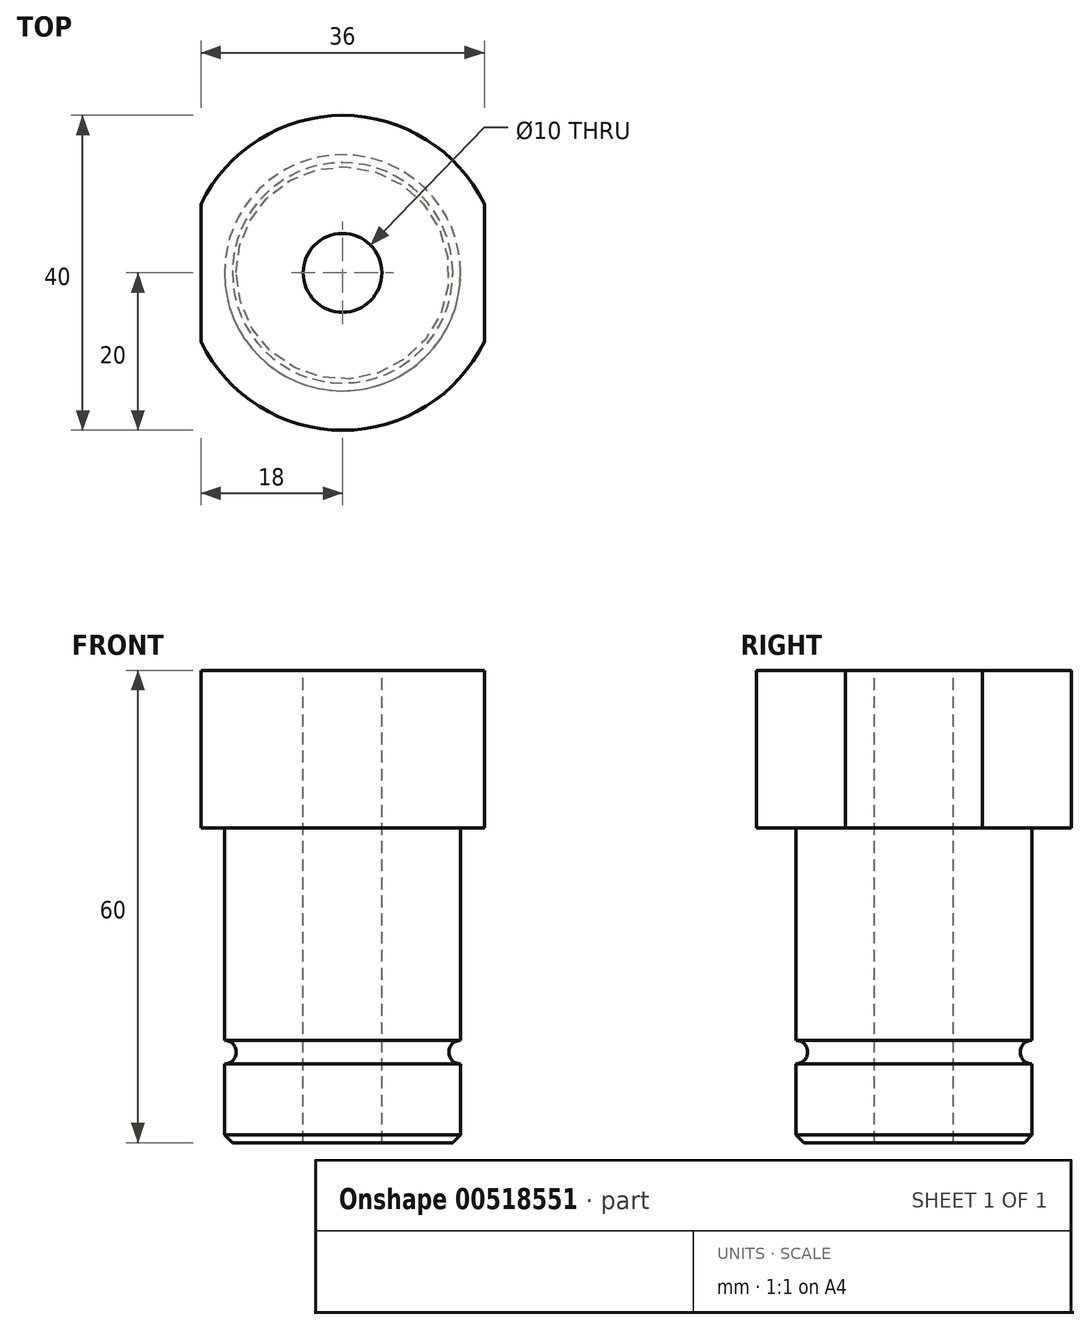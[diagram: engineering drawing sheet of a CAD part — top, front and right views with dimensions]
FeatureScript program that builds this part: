
annotation { "Feature Type Name" : "Feature", "Feature Type Description" : "" }
export const myFeature = defineFeature(function(context is Context, id is Id, definition is map)
    precondition{}
    {
        {
            var Q0;
            Q0=qCreatedBy(makeId("Top.planeOp"),FACE);
            var sketch = newSketch(context, id + "F0", { "sketchPlane" : qUnion([Q0])});
            skCircle(sketch, "E0", {"center": v(0, 0) * mm, "radius": 15 * mm});
            skSolve(sketch);
        }
        {
            var Q0;
            Q0 = qSketchRegion(id + "F0", true);
            extrude(context, id + "F1", {"entities" : qUnion([Q0]), "depth" : 40 * mm, "offsetDistance" : 25 * mm});
        }
        {
            var Q0;
            Q0=makeQuery(id+"F1.opExtrude","CAP_FACE",FACE,{"disambiguationData":[OSD([sQuery(id+"F0.wireOp",EDGE,"E0")])],"isStart":false});
            var sketch = newSketch(context, id + "F2", { "sketchPlane" : qUnion([Q0])});
            skCircle(sketch, "E1", {"center": v(0, 0) * mm, "radius": 20 * mm});
            skSolve(sketch);
        }
        {
            var Q0;
            Q0=makeQuery(id+"F1.opExtrude","CAP_FACE",FACE,{"disambiguationData":[OSD([sQuery(id+"F0.wireOp",EDGE,"E0")])],"isStart":true});
            cPlane(context, id + "F3", {"entities" : qUnion([Q0]), "cplaneType" : CPlaneType.OFFSET, "offset" : 60 * mm, "oppositeDirection" : true, "width" : 150 * mm, "height" : 150 * mm});
        }
        {
            var Q0;
            Q0 = qSketchRegion(id + "F2", true);
            var Q1;
            Q1=qCreatedBy(id+"F3.planeOp",FACE);
            extrude(context, id + "F4", {"entities" : qUnion([Q0]), "operationType" : NewBodyOperationType.ADD, "endBound" : BoundingType.UP_TO_SURFACE, "depth" : 25 * mm, "endBoundEntityFace" : qUnion([Q1]), "offsetDistance" : 25 * mm});
        }
        {
            var Q0;
            Q0=makeQuery(id+"F4.opExtrude","CAP_FACE",FACE,{"disambiguationData":[OSD([sQuery(id+"F2.wireOp",EDGE,"E1")])],"isStart":false});
            var sketch = newSketch(context, id + "F5", { "sketchPlane" : qUnion([Q0])});
            skCircle(sketch, "E2", {"center": v(0, 0) * mm, "radius": 5 * mm});
            skSolve(sketch);
        }
        {
            var Q0;
            Q0 = qSketchRegion(id + "F5", true);
            extrude(context, id + "F6", {"entities" : qUnion([Q0]), "operationType" : NewBodyOperationType.REMOVE, "endBound" : BoundingType.THROUGH_ALL, "oppositeDirection" : true, "depth" : 25 * mm, "offsetDistance" : 25 * mm});
        }
        {
            var Q0;
            Q0=makeQuery(id+"F4.opExtrude","CAP_FACE",FACE,{"disambiguationData":[OSD([sQuery(id+"F2.wireOp",EDGE,"E1")])],"isStart":false});
            var sketch = newSketch(context, id + "F7", { "sketchPlane" : qUnion([Q0])});
            skLineSegment(sketch, "E3", {"start": v(-18, 0) * mm, "end": v(18, 0) * mm});
            skLineSegment(sketch, "E4", {"start": v(-18, -8.72) * mm, "end": v(-18, 8.72) * mm});
            skLineSegment(sketch, "E5", {"start": v(18, 8.72) * mm, "end": v(18, -8.72) * mm});
            skSolve(sketch);
        }
        {
            var Q0;
            Q0 = qSketchRegion(id + "F7", true);
            var Q1;
            {var subQ0=sQuery(id+"F7.wireOp",EDGE,"E4");var subQ1=makeQuery(id+"F7.imprint","INTERSECT",VERTEX,{"derivedFrom":[sQuery(id+"F7.wireOp",EDGE,"E3"),subQ0]});Q1=makeQuery(id+"F7.imprint","IMPRINT",FACE,{"disambiguationData":[TD([[makeQuery(id+"F7.imprint","IMPRINT",EDGE,{"disambiguationData":[TD([[subQ1,1.0]])],"derivedFrom":subQ0}),1.0]])]});}
            var Q2;
            {var subQ0=sQuery(id+"F7.wireOp",EDGE,"E5");var subQ1=makeQuery(id+"F7.imprint","INTERSECT",VERTEX,{"derivedFrom":[sQuery(id+"F7.wireOp",EDGE,"E3"),subQ0]});Q2=makeQuery(id+"F7.imprint","IMPRINT",FACE,{"disambiguationData":[TD([[makeQuery(id+"F7.imprint","IMPRINT",EDGE,{"disambiguationData":[TD([[subQ1,1.0]])],"derivedFrom":subQ0}),1.0]])]});}
            extrude(context, id + "F8", {"entities" : qUnion([Q0, Q1, Q2]), "operationType" : NewBodyOperationType.REMOVE, "endBound" : BoundingType.THROUGH_ALL, "oppositeDirection" : true, "depth" : 25 * mm, "offsetDistance" : 25 * mm});
        }
        {
            var Q0;
            Q0=qCreatedBy(makeId("Right.planeOp"),FACE);
            var sketch = newSketch(context, id + "F9", { "sketchPlane" : qUnion([Q0])});
            skCircle(sketch, "E6", {"center": v(-15, 11.5) * mm, "radius": 1.5 * mm});
            skLineSegment(sketch, "E7", {"start": v(0, 60.3) * mm, "end": v(0, -4.76) * mm, "construction": true});
            skSolve(sketch);
        }
        {
            var Q0;
            Q0 = qSketchRegion(id + "F9", true);
            var Q1;
            Q1=makeQuery(id+"F1.opExtrude","SWEPT_FACE",FACE,{"disambiguationData":[OSD([sQuery(id+"F0.wireOp",EDGE,"E0")])]});
            revolve(context, id + "F10", {"operationType" : NewBodyOperationType.REMOVE, "entities" : qUnion([Q0]), "axis" : qUnion([Q1]), "revolveType" : RevolveType.FULL, "oppositeDirection" : true});
        }
        {
            var Q0;
            Q0=makeQuery(id+"F1.opExtrude","CAP_EDGE",EDGE,{"disambiguationData":[OSD([sQuery(id+"F0.wireOp",EDGE,"E0")])],"isStart":true});
            chamfer(context, id + "F11", {"entities" : qUnion([Q0]), "width" : 1 * mm, "tangentPropagation" : true});
        }
    });
